# Revit family: 1900H Corner Perchpad
name_source: partatom
category: Casework
revit_build: Autodesk Revit 2016 (Build: 20150220_1215(x64)
units: mm (PartAtom-declared; Revit-internal decimal feet)

## family parameters
Always vertical = Yes
Cut with Voids When Loaded = No
OmniClass Number = 23.40.35.00
OmniClass Title = Casework
Room Calculation Point = No
Shared = No
Work Plane-Based = No

## types (1)
- LW2019CPP
    1m = No
    2m = Yes
    AssetType = Fixed
    Carcass Material = MFC
    Depth = 2000 mm  [stored 6.56168 ft]
    DurationUnit = Years
    Finish = Matt
    Height = 1900 mm  [stored 6.2336 ft]
    ManufactureName = Bisley
    Manufacturer = Bisley
    ManufacturerURL = www.bisley.com
    Material = MFC
    Model = Abode
    ModelReference = LW2019CPP
    NBSDescription = General fittings, furnishings and equipment system
    NBSReference = 45-35-80/380
    Name = 1900H Corner Perch Pad
    NominalHeight = 1900 mm  [stored 6.2336 ft]
    NominalLength = 2000 mm  [stored 6.56168 ft]
    NominalWidth = 2000 mm  [stored 6.56168 ft]
    SustainabilityPerformance = FSC Approved
    URL = www.bisley.com
    Uniclass2015Code = Pr_40_30_78_48
    Uniclass2015Title = Lockers
    Uniclass2015Version = 3.1
    WarrantyDescription = 5 Years Parts & Labour
    WarrantyDurationLabour = 5
    WarrantyDurationParts = 5
    WarrantyDurationUnit = Years
    WarrantyGuarantorLabour = www.bisley.com
    WarrantyGuarantorParts = www.bisley.com
    Width = 2000 mm  [stored 6.56168 ft]

note: [stored X ft] marks values corroborated as IEEE doubles in the binary element streams (Revit-internal decimal feet)

## geometry (parser evidence)
native form markers: Sweep x5
no freeform markers — native parametric forms only
